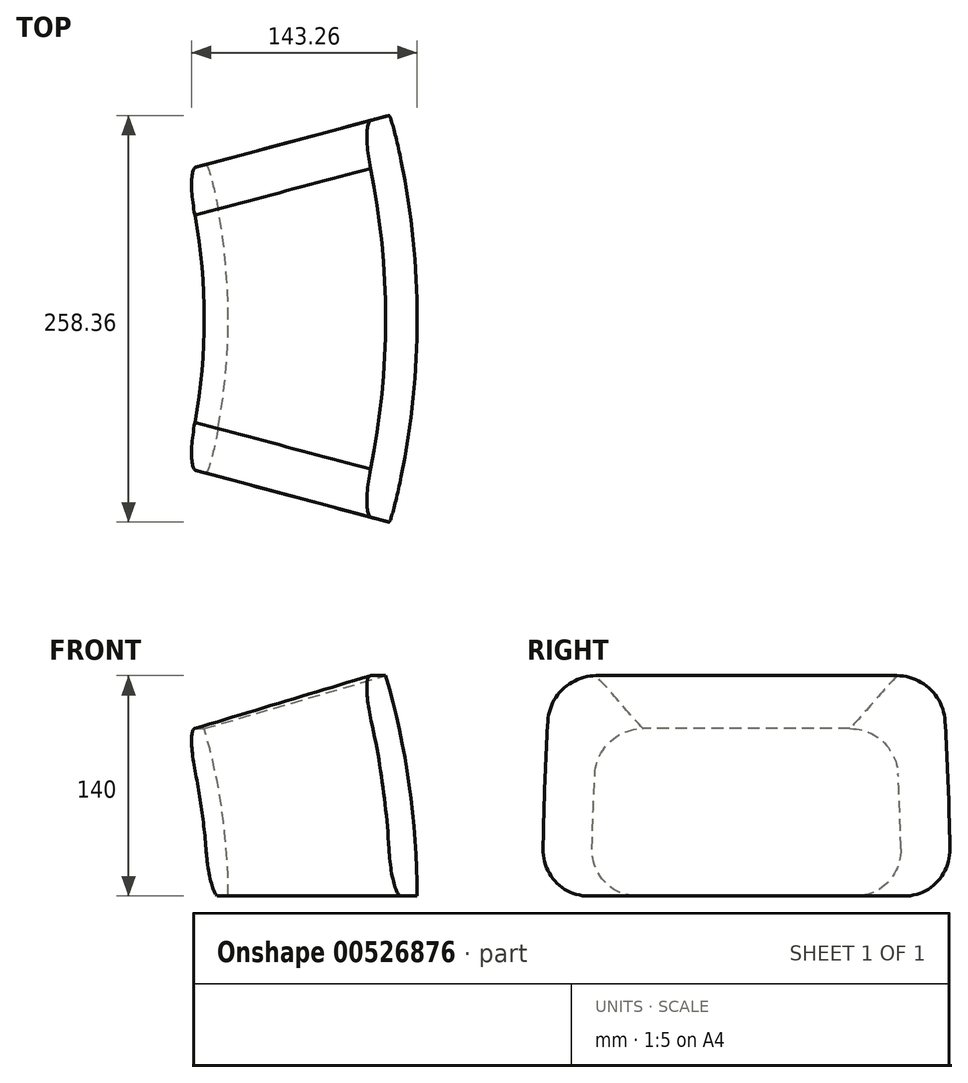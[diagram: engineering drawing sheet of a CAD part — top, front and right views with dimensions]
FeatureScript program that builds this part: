
annotation { "Feature Type Name" : "Feature", "Feature Type Description" : "" }
export const myFeature = defineFeature(function(context is Context, id is Id, definition is map)
    precondition{}
    {
        {
            var Q0;
            Q0=qCreatedBy(makeId("Front.planeOp"),FACE);
            var sketch = newSketch(context, id + "F0", { "sketchPlane" : qUnion([Q0])});
            skArc(sketch, "E0", {"start": v(500, 0) * mm, "mid": v(494.97, 70.71) * mm, "end": v(480, 140) * mm});
            skArc(sketch, "E1", {"start": v(380, 0) * mm, "mid": v(376.18, 53.74) * mm, "end": v(364.8, 106.4) * mm});
            skLineSegment(sketch, "E2", {"start": v(380, 0) * mm, "end": v(500, 0) * mm});
            skLineSegment(sketch, "E3", {"start": v(364.8, 106.4) * mm, "end": v(480, 140) * mm});
            skLineSegment(sketch, "E4", {"start": v(0, 0) * mm, "end": v(0, 50.67) * mm, "construction": true});
            skSolve(sketch);
        }
        {
            var Q0;
            Q0 = qSketchRegion(id + "F0", true);
            var Q1;
            Q1=sQuery(id+"F0.wireOp",EDGE,"E4");
            revolve(context, id + "F1", {"entities" : qUnion([Q0]), "axis" : qUnion([Q1]), "revolveType" : RevolveType.SYMMETRIC, "angle" : 30 * degree});
        }
        {
            var Q0;
            Q0=makeQuery(id+"F1.opRevolve","CAP_EDGE",EDGE,{"disambiguationData":[OSD([sQuery(id+"F0.wireOp",EDGE,"E3")])],"isStart":true});
            var Q1;
            Q1=makeQuery(id+"F1.opRevolve","CAP_EDGE",EDGE,{"disambiguationData":[OSD([sQuery(id+"F0.wireOp",EDGE,"E2")])],"isStart":true});
            var Q2;
            Q2=makeQuery(id+"F1.opRevolve","CAP_EDGE",EDGE,{"disambiguationData":[OSD([sQuery(id+"F0.wireOp",EDGE,"E2")])],"isStart":false});
            var Q3;
            Q3=makeQuery(id+"F1.opRevolve","CAP_EDGE",EDGE,{"disambiguationData":[OSD([sQuery(id+"F0.wireOp",EDGE,"E3")])],"isStart":false});
            fillet(context, id + "F2", {"entities" : qUnion([Q0, Q1, Q2, Q3]), "radius" : 30 * mm, "tangentPropagation" : true, "allowEdgeOverflow" : false});
        }
    });
